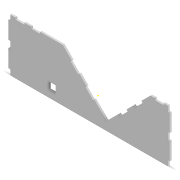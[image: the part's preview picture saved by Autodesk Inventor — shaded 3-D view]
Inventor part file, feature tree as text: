
AUTODESK INVENTOR PART (.ipt)
format: ipt  version: 2022 (Build 260153000, 153)  size: 196,096 bytes
history: native  units: mm
features: reference x5, other x5, sketch x3, extrude x2, projected_geometry x1
ambient origin geometry x8: Origin, YZ Plane, XZ Plane, XY Plane, X Axis, Y Axis, Z Axis, Center Point
bodies: Solid1 (feature_tree)
feature tree (16):
  extrude  "Extrusion1"  Depth=20.0mm
  sketch  "Sketch2"  dims[d5=20.0mm d6=20.0mm]
  extrude  "Extrusion3"  Depth=20.0mm
  sketch  "Sketch1"  dims[d0=5.0mm d1=0.0mm d4=20.0mm]
  reference  "Reference1"
  reference  "Reference2"
  reference  "Reference3"
  reference  "Reference4"
  reference  "Reference5"
  sketch  "Sketch4"  dims[d7=110.0mm d8=10.0mm d9=0.0mm]
  projected_geometry  "Projected Loop2"
  parser-record x1  (decoder bookkeeping rows leaked as tree rows — omitted from the tree; the rows remain in map.json)
  other  "Ensamble caja.iam"
  other  "Modelo base:1"
  other  "Lateral:2"
  other  "Lateral:1"
note: 1 file-system path scrubbed to <path> (originals preserved in map.json)
